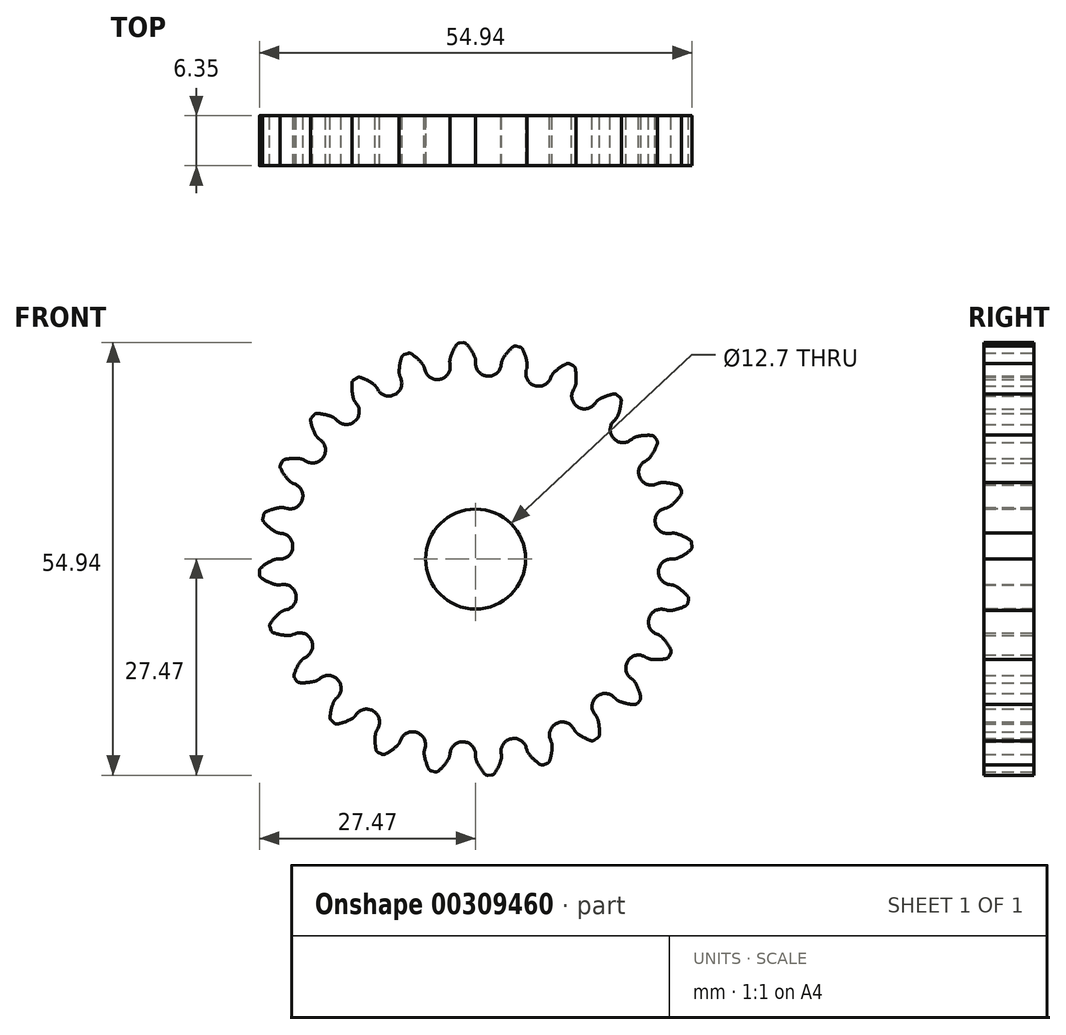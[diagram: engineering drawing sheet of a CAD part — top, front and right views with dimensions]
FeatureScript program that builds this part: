
annotation { "Feature Type Name" : "Feature", "Feature Type Description" : "" }
export const myFeature = defineFeature(function(context is Context, id is Id, definition is map)
    precondition{}
    {
        {
            var Q0;
            Q0=qCreatedBy(makeId("Front.planeOp"),FACE);
            var sketch = newSketch(context, id + "F0", { "sketchPlane" : qUnion([Q0])});
            skArc(sketch, "E0", {"start": v(-4.52, 22.84) * mm, "mid": v(-4.54, 22.83) * mm, "end": v(-4.57, 22.83) * mm});
            skArc(sketch, "E1", {"start": v(-0.14, 25.74) * mm, "mid": v(-0.59, 26.56) * mm, "end": v(-1.15, 27.3) * mm});
            skLineSegment(sketch, "E2", {"start": v(0, 25.08) * mm, "end": v(0, 24.83) * mm});
            skLineSegment(sketch, "E3", {"start": v(-1.56, 27.47) * mm, "end": v(-1.8, 27.46) * mm});
            skLineSegment(sketch, "E4.MirrorCS", {"start": v(-2.04, 27.44) * mm, "end": v(-1.8, 27.46) * mm});
            skArc(sketch, "E5.MirrorCS", {"start": v(-3.22, 25.54) * mm, "mid": v(-2.88, 26.4) * mm, "end": v(-2.43, 27.22) * mm});
            skLineSegment(sketch, "E6.MirrorCS", {"start": v(-3.27, 24.87) * mm, "end": v(-3.24, 24.62) * mm});
            skPoint(sketch, "E7.visualSharp", {"position": v(-3.04, 23.08) * mm});
            skArc(sketch, "E7.filletArc", {"start": v(-4.52, 22.84) * mm, "mid": v(-3.53, 23.47) * mm, "end": v(-3.24, 24.62) * mm});
            skPoint(sketch, "E8.visualSharp", {"position": v(0, 23.28) * mm});
            skArc(sketch, "E8.filletArc", {"start": v(0, 24.83) * mm, "mid": v(0.43, 23.73) * mm, "end": v(1.5, 23.23) * mm});
            skPoint(sketch, "E9.visualSharp", {"position": v(0, 25.4) * mm});
            skArc(sketch, "E9.filletArc", {"start": v(0, 25.08) * mm, "mid": v(-0.04, 25.42) * mm, "end": v(-0.14, 25.74) * mm});
            skPoint(sketch, "E10.visualSharp", {"position": v(-3.32, 25.18) * mm});
            skArc(sketch, "E10.filletArc", {"start": v(-3.22, 25.54) * mm, "mid": v(-3.28, 25.2) * mm, "end": v(-3.27, 24.87) * mm});
            skPoint(sketch, "E11.visualSharp", {"position": v(-2.28, 27.43) * mm});
            skArc(sketch, "E11.filletArc", {"start": v(-2.04, 27.44) * mm, "mid": v(-2.26, 27.38) * mm, "end": v(-2.43, 27.22) * mm});
            skPoint(sketch, "E12.visualSharp", {"position": v(-1.32, 27.49) * mm});
            skArc(sketch, "E12.filletArc", {"start": v(-1.15, 27.3) * mm, "mid": v(-1.33, 27.44) * mm, "end": v(-1.56, 27.47) * mm});
            skArc(sketch, "E13.1.0", {"start": v(-10.27, 20.89) * mm, "mid": v(-9.48, 21.76) * mm, "end": v(-9.5, 22.94) * mm});
            skLineSegment(sketch, "E13.1.1", {"start": v(-9.6, 23.17) * mm, "end": v(-9.5, 22.94) * mm});
            skArc(sketch, "E13.1.2", {"start": v(-9.72, 23.84) * mm, "mid": v(-9.7, 23.5) * mm, "end": v(-9.6, 23.17) * mm});
            skArc(sketch, "E13.1.3", {"start": v(-9.07, 25.98) * mm, "mid": v(-9.27, 25.86) * mm, "end": v(-9.39, 25.66) * mm});
            skArc(sketch, "E13.1.4", {"start": v(-9.72, 23.84) * mm, "mid": v(-9.62, 24.76) * mm, "end": v(-9.39, 25.66) * mm});
            skLineSegment(sketch, "E13.1.5", {"start": v(-9.07, 25.98) * mm, "end": v(-8.84, 26.06) * mm});
            skLineSegment(sketch, "E13.1.6", {"start": v(-8.62, 26.13) * mm, "end": v(-8.84, 26.06) * mm});
            skArc(sketch, "E13.1.7", {"start": v(-8.17, 26.07) * mm, "mid": v(-8.39, 26.16) * mm, "end": v(-8.62, 26.13) * mm});
            skArc(sketch, "E13.1.8", {"start": v(-6.8, 24.83) * mm, "mid": v(-7.44, 25.5) * mm, "end": v(-8.17, 26.07) * mm});
            skArc(sketch, "E13.1.9", {"start": v(-6.5, 24.23) * mm, "mid": v(-6.61, 24.54) * mm, "end": v(-6.8, 24.83) * mm});
            skLineSegment(sketch, "E13.1.10", {"start": v(-6.5, 24.23) * mm, "end": v(-6.43, 23.98) * mm});
            skArc(sketch, "E13.1.11", {"start": v(-6.43, 23.98) * mm, "mid": v(-5.72, 23.04) * mm, "end": v(-4.57, 22.83) * mm});
            skArc(sketch, "E13.2.0", {"start": v(-15.33, 17.52) * mm, "mid": v(-14.8, 18.57) * mm, "end": v(-15.11, 19.7) * mm});
            skLineSegment(sketch, "E13.2.1", {"start": v(-15.27, 19.9) * mm, "end": v(-15.11, 19.7) * mm});
            skArc(sketch, "E13.2.2", {"start": v(-15.56, 20.5) * mm, "mid": v(-15.45, 20.19) * mm, "end": v(-15.27, 19.9) * mm});
            skArc(sketch, "E13.2.3", {"start": v(-15.49, 22.75) * mm, "mid": v(-15.64, 22.58) * mm, "end": v(-15.7, 22.36) * mm});
            skArc(sketch, "E13.2.4", {"start": v(-15.56, 20.5) * mm, "mid": v(-15.7, 21.43) * mm, "end": v(-15.7, 22.36) * mm});
            skLineSegment(sketch, "E13.2.5", {"start": v(-15.49, 22.75) * mm, "end": v(-15.29, 22.88) * mm});
            skLineSegment(sketch, "E13.2.6", {"start": v(-15.09, 23.01) * mm, "end": v(-15.29, 22.88) * mm});
            skArc(sketch, "E13.2.7", {"start": v(-14.64, 23.07) * mm, "mid": v(-14.87, 23.1) * mm, "end": v(-15.09, 23.01) * mm});
            skArc(sketch, "E13.2.8", {"start": v(-13, 22.22) * mm, "mid": v(-13.79, 22.7) * mm, "end": v(-14.64, 23.07) * mm});
            skArc(sketch, "E13.2.9", {"start": v(-12.54, 21.72) * mm, "mid": v(-12.74, 22) * mm, "end": v(-13, 22.22) * mm});
            skLineSegment(sketch, "E13.2.10", {"start": v(-12.54, 21.72) * mm, "end": v(-12.41, 21.5) * mm});
            skArc(sketch, "E13.2.11", {"start": v(-12.41, 21.5) * mm, "mid": v(-11.5, 20.77) * mm, "end": v(-10.32, 20.87) * mm});
            skArc(sketch, "E13.3.0", {"start": v(-19.34, 12.95) * mm, "mid": v(-19.1, 14.1) * mm, "end": v(-19.7, 15.11) * mm});
            skLineSegment(sketch, "E13.3.1", {"start": v(-19.9, 15.27) * mm, "end": v(-19.7, 15.11) * mm});
            skArc(sketch, "E13.3.2", {"start": v(-20.33, 15.78) * mm, "mid": v(-20.14, 15.5) * mm, "end": v(-19.9, 15.27) * mm});
            skArc(sketch, "E13.3.3", {"start": v(-20.84, 17.96) * mm, "mid": v(-20.95, 17.76) * mm, "end": v(-20.96, 17.53) * mm});
            skArc(sketch, "E13.3.4", {"start": v(-20.33, 15.78) * mm, "mid": v(-20.71, 16.63) * mm, "end": v(-20.96, 17.53) * mm});
            skLineSegment(sketch, "E13.3.5", {"start": v(-20.84, 17.96) * mm, "end": v(-20.69, 18.14) * mm});
            skLineSegment(sketch, "E13.3.6", {"start": v(-20.53, 18.32) * mm, "end": v(-20.69, 18.14) * mm});
            skArc(sketch, "E13.3.7", {"start": v(-20.12, 18.5) * mm, "mid": v(-20.34, 18.46) * mm, "end": v(-20.53, 18.32) * mm});
            skArc(sketch, "E13.3.8", {"start": v(-18.3, 18.1) * mm, "mid": v(-19.2, 18.36) * mm, "end": v(-20.12, 18.5) * mm});
            skArc(sketch, "E13.3.9", {"start": v(-17.73, 17.73) * mm, "mid": v(-18, 17.95) * mm, "end": v(-18.3, 18.1) * mm});
            skLineSegment(sketch, "E13.3.10", {"start": v(-17.73, 17.73) * mm, "end": v(-17.56, 17.56) * mm});
            skArc(sketch, "E13.3.11", {"start": v(-17.56, 17.56) * mm, "mid": v(-16.48, 17.09) * mm, "end": v(-15.37, 17.49) * mm});
            skArc(sketch, "E13.4.0", {"start": v(-22.04, 7.5) * mm, "mid": v(-22.1, 8.68) * mm, "end": v(-22.94, 9.5) * mm});
            skLineSegment(sketch, "E13.4.1", {"start": v(-23.17, 9.6) * mm, "end": v(-22.94, 9.5) * mm});
            skArc(sketch, "E13.4.2", {"start": v(-23.73, 9.98) * mm, "mid": v(-23.47, 9.76) * mm, "end": v(-23.17, 9.6) * mm});
            skArc(sketch, "E13.4.3", {"start": v(-24.78, 11.96) * mm, "mid": v(-24.84, 11.73) * mm, "end": v(-24.78, 11.5) * mm});
            skArc(sketch, "E13.4.4", {"start": v(-23.73, 9.98) * mm, "mid": v(-24.31, 10.7) * mm, "end": v(-24.78, 11.5) * mm});
            skLineSegment(sketch, "E13.4.5", {"start": v(-24.78, 11.96) * mm, "end": v(-24.68, 12.17) * mm});
            skLineSegment(sketch, "E13.4.6", {"start": v(-24.57, 12.38) * mm, "end": v(-24.68, 12.17) * mm});
            skArc(sketch, "E13.4.7", {"start": v(-24.22, 12.66) * mm, "mid": v(-24.43, 12.56) * mm, "end": v(-24.57, 12.38) * mm});
            skArc(sketch, "E13.4.8", {"start": v(-22.36, 12.75) * mm, "mid": v(-23.3, 12.77) * mm, "end": v(-24.22, 12.66) * mm});
            skArc(sketch, "E13.4.9", {"start": v(-21.72, 12.54) * mm, "mid": v(-22.03, 12.68) * mm, "end": v(-22.36, 12.75) * mm});
            skLineSegment(sketch, "E13.4.10", {"start": v(-21.72, 12.54) * mm, "end": v(-21.5, 12.41) * mm});
            skArc(sketch, "E13.4.11", {"start": v(-21.5, 12.41) * mm, "mid": v(-20.34, 12.24) * mm, "end": v(-19.37, 12.91) * mm});
            skArc(sketch, "E13.5.0", {"start": v(-23.23, 1.55) * mm, "mid": v(-23.59, 2.67) * mm, "end": v(-24.62, 3.24) * mm});
            skLineSegment(sketch, "E13.5.1", {"start": v(-24.87, 3.27) * mm, "end": v(-24.62, 3.24) * mm});
            skArc(sketch, "E13.5.2", {"start": v(-25.5, 3.5) * mm, "mid": v(-25.2, 3.35) * mm, "end": v(-24.87, 3.27) * mm});
            skArc(sketch, "E13.5.3", {"start": v(-27.03, 5.14) * mm, "mid": v(-27.03, 4.9) * mm, "end": v(-26.92, 4.7) * mm});
            skArc(sketch, "E13.5.4", {"start": v(-25.5, 3.5) * mm, "mid": v(-26.25, 4.05) * mm, "end": v(-26.92, 4.7) * mm});
            skLineSegment(sketch, "E13.5.5", {"start": v(-27.03, 5.14) * mm, "end": v(-26.99, 5.37) * mm});
            skLineSegment(sketch, "E13.5.6", {"start": v(-26.94, 5.6) * mm, "end": v(-26.99, 5.37) * mm});
            skArc(sketch, "E13.5.7", {"start": v(-26.67, 5.96) * mm, "mid": v(-26.85, 5.81) * mm, "end": v(-26.94, 5.6) * mm});
            skArc(sketch, "E13.5.8", {"start": v(-24.9, 6.52) * mm, "mid": v(-25.8, 6.3) * mm, "end": v(-26.67, 5.96) * mm});
            skArc(sketch, "E13.5.9", {"start": v(-24.23, 6.5) * mm, "mid": v(-24.56, 6.54) * mm, "end": v(-24.9, 6.52) * mm});
            skLineSegment(sketch, "E13.5.10", {"start": v(-24.23, 6.5) * mm, "end": v(-23.98, 6.43) * mm});
            skArc(sketch, "E13.5.11", {"start": v(-23.98, 6.43) * mm, "mid": v(-22.81, 6.56) * mm, "end": v(-22.05, 7.46) * mm});
            skArc(sketch, "E13.6.0", {"start": v(-22.84, -4.52) * mm, "mid": v(-23.47, -3.53) * mm, "end": v(-24.62, -3.24) * mm});
            skLineSegment(sketch, "E13.6.1", {"start": v(-24.87, -3.27) * mm, "end": v(-24.62, -3.24) * mm});
            skArc(sketch, "E13.6.2", {"start": v(-25.54, -3.22) * mm, "mid": v(-25.2, -3.28) * mm, "end": v(-24.87, -3.27) * mm});
            skArc(sketch, "E13.6.3", {"start": v(-27.44, -2.04) * mm, "mid": v(-27.38, -2.26) * mm, "end": v(-27.22, -2.43) * mm});
            skArc(sketch, "E13.6.4", {"start": v(-25.54, -3.22) * mm, "mid": v(-26.4, -2.88) * mm, "end": v(-27.22, -2.43) * mm});
            skLineSegment(sketch, "E13.6.5", {"start": v(-27.44, -2.04) * mm, "end": v(-27.46, -1.8) * mm});
            skLineSegment(sketch, "E13.6.6", {"start": v(-27.47, -1.56) * mm, "end": v(-27.46, -1.8) * mm});
            skArc(sketch, "E13.6.7", {"start": v(-27.3, -1.15) * mm, "mid": v(-27.44, -1.33) * mm, "end": v(-27.47, -1.56) * mm});
            skArc(sketch, "E13.6.8", {"start": v(-25.74, -0.14) * mm, "mid": v(-26.56, -0.59) * mm, "end": v(-27.3, -1.15) * mm});
            skArc(sketch, "E13.6.9", {"start": v(-25.08, 0) * mm, "mid": v(-25.42, -0.04) * mm, "end": v(-25.74, -0.14) * mm});
            skLineSegment(sketch, "E13.6.10", {"start": v(-25.08, 0) * mm, "end": v(-24.83, 0) * mm});
            skArc(sketch, "E13.6.11", {"start": v(-24.83, 0) * mm, "mid": v(-23.73, 0.43) * mm, "end": v(-23.23, 1.5) * mm});
            skArc(sketch, "E13.7.0", {"start": v(-20.89, -10.27) * mm, "mid": v(-21.76, -9.48) * mm, "end": v(-22.94, -9.5) * mm});
            skLineSegment(sketch, "E13.7.1", {"start": v(-23.17, -9.6) * mm, "end": v(-22.94, -9.5) * mm});
            skArc(sketch, "E13.7.2", {"start": v(-23.84, -9.72) * mm, "mid": v(-23.5, -9.7) * mm, "end": v(-23.17, -9.6) * mm});
            skArc(sketch, "E13.7.3", {"start": v(-25.98, -9.07) * mm, "mid": v(-25.86, -9.27) * mm, "end": v(-25.66, -9.39) * mm});
            skArc(sketch, "E13.7.4", {"start": v(-23.84, -9.72) * mm, "mid": v(-24.76, -9.62) * mm, "end": v(-25.66, -9.39) * mm});
            skLineSegment(sketch, "E13.7.5", {"start": v(-25.98, -9.07) * mm, "end": v(-26.06, -8.84) * mm});
            skLineSegment(sketch, "E13.7.6", {"start": v(-26.13, -8.62) * mm, "end": v(-26.06, -8.84) * mm});
            skArc(sketch, "E13.7.7", {"start": v(-26.07, -8.17) * mm, "mid": v(-26.16, -8.39) * mm, "end": v(-26.13, -8.62) * mm});
            skArc(sketch, "E13.7.8", {"start": v(-24.83, -6.8) * mm, "mid": v(-25.5, -7.44) * mm, "end": v(-26.07, -8.17) * mm});
            skArc(sketch, "E13.7.9", {"start": v(-24.23, -6.5) * mm, "mid": v(-24.54, -6.61) * mm, "end": v(-24.83, -6.8) * mm});
            skLineSegment(sketch, "E13.7.10", {"start": v(-24.23, -6.5) * mm, "end": v(-23.98, -6.43) * mm});
            skArc(sketch, "E13.7.11", {"start": v(-23.98, -6.43) * mm, "mid": v(-23.04, -5.72) * mm, "end": v(-22.83, -4.57) * mm});
            skArc(sketch, "E13.8.0", {"start": v(-17.52, -15.33) * mm, "mid": v(-18.57, -14.8) * mm, "end": v(-19.7, -15.11) * mm});
            skLineSegment(sketch, "E13.8.1", {"start": v(-19.9, -15.27) * mm, "end": v(-19.7, -15.11) * mm});
            skArc(sketch, "E13.8.2", {"start": v(-20.5, -15.56) * mm, "mid": v(-20.19, -15.45) * mm, "end": v(-19.9, -15.27) * mm});
            skArc(sketch, "E13.8.3", {"start": v(-22.75, -15.49) * mm, "mid": v(-22.58, -15.64) * mm, "end": v(-22.36, -15.7) * mm});
            skArc(sketch, "E13.8.4", {"start": v(-20.5, -15.56) * mm, "mid": v(-21.43, -15.7) * mm, "end": v(-22.36, -15.7) * mm});
            skLineSegment(sketch, "E13.8.5", {"start": v(-22.75, -15.49) * mm, "end": v(-22.88, -15.29) * mm});
            skLineSegment(sketch, "E13.8.6", {"start": v(-23.01, -15.09) * mm, "end": v(-22.88, -15.29) * mm});
            skArc(sketch, "E13.8.7", {"start": v(-23.07, -14.64) * mm, "mid": v(-23.1, -14.87) * mm, "end": v(-23.01, -15.09) * mm});
            skArc(sketch, "E13.8.8", {"start": v(-22.22, -13) * mm, "mid": v(-22.7, -13.79) * mm, "end": v(-23.07, -14.64) * mm});
            skArc(sketch, "E13.8.9", {"start": v(-21.72, -12.54) * mm, "mid": v(-22, -12.74) * mm, "end": v(-22.22, -13) * mm});
            skLineSegment(sketch, "E13.8.10", {"start": v(-21.72, -12.54) * mm, "end": v(-21.5, -12.41) * mm});
            skArc(sketch, "E13.8.11", {"start": v(-21.5, -12.41) * mm, "mid": v(-20.77, -11.5) * mm, "end": v(-20.87, -10.32) * mm});
            skArc(sketch, "E13.9.0", {"start": v(-12.95, -19.34) * mm, "mid": v(-14.1, -19.1) * mm, "end": v(-15.11, -19.7) * mm});
            skLineSegment(sketch, "E13.9.1", {"start": v(-15.27, -19.9) * mm, "end": v(-15.11, -19.7) * mm});
            skArc(sketch, "E13.9.2", {"start": v(-15.78, -20.33) * mm, "mid": v(-15.5, -20.14) * mm, "end": v(-15.27, -19.9) * mm});
            skArc(sketch, "E13.9.3", {"start": v(-17.96, -20.84) * mm, "mid": v(-17.76, -20.95) * mm, "end": v(-17.53, -20.96) * mm});
            skArc(sketch, "E13.9.4", {"start": v(-15.78, -20.33) * mm, "mid": v(-16.63, -20.71) * mm, "end": v(-17.53, -20.96) * mm});
            skLineSegment(sketch, "E13.9.5", {"start": v(-17.96, -20.84) * mm, "end": v(-18.14, -20.69) * mm});
            skLineSegment(sketch, "E13.9.6", {"start": v(-18.32, -20.53) * mm, "end": v(-18.14, -20.69) * mm});
            skArc(sketch, "E13.9.7", {"start": v(-18.5, -20.12) * mm, "mid": v(-18.46, -20.34) * mm, "end": v(-18.32, -20.53) * mm});
            skArc(sketch, "E13.9.8", {"start": v(-18.1, -18.3) * mm, "mid": v(-18.36, -19.2) * mm, "end": v(-18.5, -20.12) * mm});
            skArc(sketch, "E13.9.9", {"start": v(-17.73, -17.73) * mm, "mid": v(-17.95, -18) * mm, "end": v(-18.1, -18.3) * mm});
            skLineSegment(sketch, "E13.9.10", {"start": v(-17.73, -17.73) * mm, "end": v(-17.56, -17.56) * mm});
            skArc(sketch, "E13.9.11", {"start": v(-17.56, -17.56) * mm, "mid": v(-17.09, -16.48) * mm, "end": v(-17.49, -15.37) * mm});
            skArc(sketch, "E13.10.0", {"start": v(-7.5, -22.04) * mm, "mid": v(-8.68, -22.1) * mm, "end": v(-9.5, -22.94) * mm});
            skLineSegment(sketch, "E13.10.1", {"start": v(-9.6, -23.17) * mm, "end": v(-9.5, -22.94) * mm});
            skArc(sketch, "E13.10.2", {"start": v(-9.98, -23.73) * mm, "mid": v(-9.76, -23.47) * mm, "end": v(-9.6, -23.17) * mm});
            skArc(sketch, "E13.10.3", {"start": v(-11.96, -24.78) * mm, "mid": v(-11.73, -24.84) * mm, "end": v(-11.5, -24.78) * mm});
            skArc(sketch, "E13.10.4", {"start": v(-9.98, -23.73) * mm, "mid": v(-10.7, -24.31) * mm, "end": v(-11.5, -24.78) * mm});
            skLineSegment(sketch, "E13.10.5", {"start": v(-11.96, -24.78) * mm, "end": v(-12.17, -24.68) * mm});
            skLineSegment(sketch, "E13.10.6", {"start": v(-12.38, -24.57) * mm, "end": v(-12.17, -24.68) * mm});
            skArc(sketch, "E13.10.7", {"start": v(-12.66, -24.22) * mm, "mid": v(-12.56, -24.43) * mm, "end": v(-12.38, -24.57) * mm});
            skArc(sketch, "E13.10.8", {"start": v(-12.75, -22.36) * mm, "mid": v(-12.77, -23.3) * mm, "end": v(-12.66, -24.22) * mm});
            skArc(sketch, "E13.10.9", {"start": v(-12.54, -21.72) * mm, "mid": v(-12.68, -22.03) * mm, "end": v(-12.75, -22.36) * mm});
            skLineSegment(sketch, "E13.10.10", {"start": v(-12.54, -21.72) * mm, "end": v(-12.41, -21.5) * mm});
            skArc(sketch, "E13.10.11", {"start": v(-12.41, -21.5) * mm, "mid": v(-12.24, -20.34) * mm, "end": v(-12.91, -19.37) * mm});
            skArc(sketch, "E13.11.0", {"start": v(-1.55, -23.23) * mm, "mid": v(-2.67, -23.59) * mm, "end": v(-3.24, -24.62) * mm});
            skLineSegment(sketch, "E13.11.1", {"start": v(-3.27, -24.87) * mm, "end": v(-3.24, -24.62) * mm});
            skArc(sketch, "E13.11.2", {"start": v(-3.5, -25.5) * mm, "mid": v(-3.35, -25.2) * mm, "end": v(-3.27, -24.87) * mm});
            skArc(sketch, "E13.11.3", {"start": v(-5.14, -27.03) * mm, "mid": v(-4.9, -27.03) * mm, "end": v(-4.7, -26.92) * mm});
            skArc(sketch, "E13.11.4", {"start": v(-3.5, -25.5) * mm, "mid": v(-4.05, -26.25) * mm, "end": v(-4.7, -26.92) * mm});
            skLineSegment(sketch, "E13.11.5", {"start": v(-5.14, -27.03) * mm, "end": v(-5.37, -26.99) * mm});
            skLineSegment(sketch, "E13.11.6", {"start": v(-5.6, -26.94) * mm, "end": v(-5.37, -26.99) * mm});
            skArc(sketch, "E13.11.7", {"start": v(-5.96, -26.67) * mm, "mid": v(-5.81, -26.85) * mm, "end": v(-5.6, -26.94) * mm});
            skArc(sketch, "E13.11.8", {"start": v(-6.52, -24.9) * mm, "mid": v(-6.3, -25.8) * mm, "end": v(-5.96, -26.67) * mm});
            skArc(sketch, "E13.11.9", {"start": v(-6.5, -24.23) * mm, "mid": v(-6.54, -24.56) * mm, "end": v(-6.52, -24.9) * mm});
            skLineSegment(sketch, "E13.11.10", {"start": v(-6.5, -24.23) * mm, "end": v(-6.43, -23.98) * mm});
            skArc(sketch, "E13.11.11", {"start": v(-6.43, -23.98) * mm, "mid": v(-6.56, -22.81) * mm, "end": v(-7.46, -22.05) * mm});
            skArc(sketch, "E13.12.0", {"start": v(4.52, -22.84) * mm, "mid": v(3.53, -23.47) * mm, "end": v(3.24, -24.62) * mm});
            skLineSegment(sketch, "E13.12.1", {"start": v(3.27, -24.87) * mm, "end": v(3.24, -24.62) * mm});
            skArc(sketch, "E13.12.2", {"start": v(3.22, -25.54) * mm, "mid": v(3.28, -25.2) * mm, "end": v(3.27, -24.87) * mm});
            skArc(sketch, "E13.12.3", {"start": v(2.04, -27.44) * mm, "mid": v(2.26, -27.38) * mm, "end": v(2.43, -27.22) * mm});
            skArc(sketch, "E13.12.4", {"start": v(3.22, -25.54) * mm, "mid": v(2.88, -26.4) * mm, "end": v(2.43, -27.22) * mm});
            skLineSegment(sketch, "E13.12.5", {"start": v(2.04, -27.44) * mm, "end": v(1.8, -27.46) * mm});
            skLineSegment(sketch, "E13.12.6", {"start": v(1.56, -27.47) * mm, "end": v(1.8, -27.46) * mm});
            skArc(sketch, "E13.12.7", {"start": v(1.15, -27.3) * mm, "mid": v(1.33, -27.44) * mm, "end": v(1.56, -27.47) * mm});
            skArc(sketch, "E13.12.8", {"start": v(0.14, -25.74) * mm, "mid": v(0.59, -26.56) * mm, "end": v(1.15, -27.3) * mm});
            skArc(sketch, "E13.12.9", {"start": v(0, -25.08) * mm, "mid": v(0.04, -25.42) * mm, "end": v(0.14, -25.74) * mm});
            skLineSegment(sketch, "E13.12.10", {"start": v(0, -25.08) * mm, "end": v(0, -24.83) * mm});
            skArc(sketch, "E13.12.11", {"start": v(0, -24.83) * mm, "mid": v(-0.43, -23.73) * mm, "end": v(-1.5, -23.23) * mm});
            skArc(sketch, "E13.13.0", {"start": v(10.27, -20.89) * mm, "mid": v(9.48, -21.76) * mm, "end": v(9.5, -22.94) * mm});
            skLineSegment(sketch, "E13.13.1", {"start": v(9.6, -23.17) * mm, "end": v(9.5, -22.94) * mm});
            skArc(sketch, "E13.13.2", {"start": v(9.72, -23.84) * mm, "mid": v(9.7, -23.5) * mm, "end": v(9.6, -23.17) * mm});
            skArc(sketch, "E13.13.3", {"start": v(9.07, -25.98) * mm, "mid": v(9.27, -25.86) * mm, "end": v(9.39, -25.66) * mm});
            skArc(sketch, "E13.13.4", {"start": v(9.72, -23.84) * mm, "mid": v(9.62, -24.76) * mm, "end": v(9.39, -25.66) * mm});
            skLineSegment(sketch, "E13.13.5", {"start": v(9.07, -25.98) * mm, "end": v(8.84, -26.06) * mm});
            skLineSegment(sketch, "E13.13.6", {"start": v(8.62, -26.13) * mm, "end": v(8.84, -26.06) * mm});
            skArc(sketch, "E13.13.7", {"start": v(8.17, -26.07) * mm, "mid": v(8.39, -26.16) * mm, "end": v(8.62, -26.13) * mm});
            skArc(sketch, "E13.13.8", {"start": v(6.8, -24.83) * mm, "mid": v(7.44, -25.5) * mm, "end": v(8.17, -26.07) * mm});
            skArc(sketch, "E13.13.9", {"start": v(6.5, -24.23) * mm, "mid": v(6.61, -24.54) * mm, "end": v(6.8, -24.83) * mm});
            skLineSegment(sketch, "E13.13.10", {"start": v(6.5, -24.23) * mm, "end": v(6.43, -23.98) * mm});
            skArc(sketch, "E13.13.11", {"start": v(6.43, -23.98) * mm, "mid": v(5.72, -23.04) * mm, "end": v(4.57, -22.83) * mm});
            skArc(sketch, "E13.14.0", {"start": v(15.33, -17.52) * mm, "mid": v(14.8, -18.57) * mm, "end": v(15.11, -19.7) * mm});
            skLineSegment(sketch, "E13.14.1", {"start": v(15.27, -19.9) * mm, "end": v(15.11, -19.7) * mm});
            skArc(sketch, "E13.14.2", {"start": v(15.56, -20.5) * mm, "mid": v(15.45, -20.19) * mm, "end": v(15.27, -19.9) * mm});
            skArc(sketch, "E13.14.3", {"start": v(15.49, -22.75) * mm, "mid": v(15.64, -22.58) * mm, "end": v(15.7, -22.36) * mm});
            skArc(sketch, "E13.14.4", {"start": v(15.56, -20.5) * mm, "mid": v(15.7, -21.43) * mm, "end": v(15.7, -22.36) * mm});
            skLineSegment(sketch, "E13.14.5", {"start": v(15.49, -22.75) * mm, "end": v(15.29, -22.88) * mm});
            skLineSegment(sketch, "E13.14.6", {"start": v(15.09, -23.01) * mm, "end": v(15.29, -22.88) * mm});
            skArc(sketch, "E13.14.7", {"start": v(14.64, -23.07) * mm, "mid": v(14.87, -23.1) * mm, "end": v(15.09, -23.01) * mm});
            skArc(sketch, "E13.14.8", {"start": v(13, -22.22) * mm, "mid": v(13.79, -22.7) * mm, "end": v(14.64, -23.07) * mm});
            skArc(sketch, "E13.14.9", {"start": v(12.54, -21.72) * mm, "mid": v(12.74, -22) * mm, "end": v(13, -22.22) * mm});
            skLineSegment(sketch, "E13.14.10", {"start": v(12.54, -21.72) * mm, "end": v(12.41, -21.5) * mm});
            skArc(sketch, "E13.14.11", {"start": v(12.41, -21.5) * mm, "mid": v(11.5, -20.77) * mm, "end": v(10.32, -20.87) * mm});
            skArc(sketch, "E13.15.0", {"start": v(19.34, -12.95) * mm, "mid": v(19.1, -14.1) * mm, "end": v(19.7, -15.11) * mm});
            skLineSegment(sketch, "E13.15.1", {"start": v(19.9, -15.27) * mm, "end": v(19.7, -15.11) * mm});
            skArc(sketch, "E13.15.2", {"start": v(20.33, -15.78) * mm, "mid": v(20.14, -15.5) * mm, "end": v(19.9, -15.27) * mm});
            skArc(sketch, "E13.15.3", {"start": v(20.84, -17.96) * mm, "mid": v(20.95, -17.76) * mm, "end": v(20.96, -17.53) * mm});
            skArc(sketch, "E13.15.4", {"start": v(20.33, -15.78) * mm, "mid": v(20.71, -16.63) * mm, "end": v(20.96, -17.53) * mm});
            skLineSegment(sketch, "E13.15.5", {"start": v(20.84, -17.96) * mm, "end": v(20.69, -18.14) * mm});
            skLineSegment(sketch, "E13.15.6", {"start": v(20.53, -18.32) * mm, "end": v(20.69, -18.14) * mm});
            skArc(sketch, "E13.15.7", {"start": v(20.12, -18.5) * mm, "mid": v(20.34, -18.46) * mm, "end": v(20.53, -18.32) * mm});
            skArc(sketch, "E13.15.8", {"start": v(18.3, -18.1) * mm, "mid": v(19.2, -18.36) * mm, "end": v(20.12, -18.5) * mm});
            skArc(sketch, "E13.15.9", {"start": v(17.73, -17.73) * mm, "mid": v(18, -17.95) * mm, "end": v(18.3, -18.1) * mm});
            skLineSegment(sketch, "E13.15.10", {"start": v(17.73, -17.73) * mm, "end": v(17.56, -17.56) * mm});
            skArc(sketch, "E13.15.11", {"start": v(17.56, -17.56) * mm, "mid": v(16.48, -17.09) * mm, "end": v(15.37, -17.49) * mm});
            skArc(sketch, "E13.16.0", {"start": v(22.04, -7.5) * mm, "mid": v(22.1, -8.68) * mm, "end": v(22.94, -9.5) * mm});
            skLineSegment(sketch, "E13.16.1", {"start": v(23.17, -9.6) * mm, "end": v(22.94, -9.5) * mm});
            skArc(sketch, "E13.16.2", {"start": v(23.73, -9.98) * mm, "mid": v(23.47, -9.76) * mm, "end": v(23.17, -9.6) * mm});
            skArc(sketch, "E13.16.3", {"start": v(24.78, -11.96) * mm, "mid": v(24.84, -11.73) * mm, "end": v(24.78, -11.5) * mm});
            skArc(sketch, "E13.16.4", {"start": v(23.73, -9.98) * mm, "mid": v(24.31, -10.7) * mm, "end": v(24.78, -11.5) * mm});
            skLineSegment(sketch, "E13.16.5", {"start": v(24.78, -11.96) * mm, "end": v(24.68, -12.17) * mm});
            skLineSegment(sketch, "E13.16.6", {"start": v(24.57, -12.38) * mm, "end": v(24.68, -12.17) * mm});
            skArc(sketch, "E13.16.7", {"start": v(24.22, -12.66) * mm, "mid": v(24.43, -12.56) * mm, "end": v(24.57, -12.38) * mm});
            skArc(sketch, "E13.16.8", {"start": v(22.36, -12.75) * mm, "mid": v(23.3, -12.77) * mm, "end": v(24.22, -12.66) * mm});
            skArc(sketch, "E13.16.9", {"start": v(21.72, -12.54) * mm, "mid": v(22.03, -12.68) * mm, "end": v(22.36, -12.75) * mm});
            skLineSegment(sketch, "E13.16.10", {"start": v(21.72, -12.54) * mm, "end": v(21.5, -12.41) * mm});
            skArc(sketch, "E13.16.11", {"start": v(21.5, -12.41) * mm, "mid": v(20.34, -12.24) * mm, "end": v(19.37, -12.91) * mm});
            skArc(sketch, "E13.17.0", {"start": v(23.23, -1.55) * mm, "mid": v(23.59, -2.67) * mm, "end": v(24.62, -3.24) * mm});
            skLineSegment(sketch, "E13.17.1", {"start": v(24.87, -3.27) * mm, "end": v(24.62, -3.24) * mm});
            skArc(sketch, "E13.17.2", {"start": v(25.5, -3.5) * mm, "mid": v(25.2, -3.35) * mm, "end": v(24.87, -3.27) * mm});
            skArc(sketch, "E13.17.3", {"start": v(27.03, -5.14) * mm, "mid": v(27.03, -4.9) * mm, "end": v(26.92, -4.7) * mm});
            skArc(sketch, "E13.17.4", {"start": v(25.5, -3.5) * mm, "mid": v(26.25, -4.05) * mm, "end": v(26.92, -4.7) * mm});
            skLineSegment(sketch, "E13.17.5", {"start": v(27.03, -5.14) * mm, "end": v(26.99, -5.37) * mm});
            skLineSegment(sketch, "E13.17.6", {"start": v(26.94, -5.6) * mm, "end": v(26.99, -5.37) * mm});
            skArc(sketch, "E13.17.7", {"start": v(26.67, -5.96) * mm, "mid": v(26.85, -5.81) * mm, "end": v(26.94, -5.6) * mm});
            skArc(sketch, "E13.17.8", {"start": v(24.9, -6.52) * mm, "mid": v(25.8, -6.3) * mm, "end": v(26.67, -5.96) * mm});
            skArc(sketch, "E13.17.9", {"start": v(24.23, -6.5) * mm, "mid": v(24.56, -6.54) * mm, "end": v(24.9, -6.52) * mm});
            skLineSegment(sketch, "E13.17.10", {"start": v(24.23, -6.5) * mm, "end": v(23.98, -6.43) * mm});
            skArc(sketch, "E13.17.11", {"start": v(23.98, -6.43) * mm, "mid": v(22.81, -6.56) * mm, "end": v(22.05, -7.46) * mm});
            skArc(sketch, "E13.18.0", {"start": v(22.84, 4.52) * mm, "mid": v(23.47, 3.53) * mm, "end": v(24.62, 3.24) * mm});
            skLineSegment(sketch, "E13.18.1", {"start": v(24.87, 3.27) * mm, "end": v(24.62, 3.24) * mm});
            skArc(sketch, "E13.18.2", {"start": v(25.54, 3.22) * mm, "mid": v(25.2, 3.28) * mm, "end": v(24.87, 3.27) * mm});
            skArc(sketch, "E13.18.3", {"start": v(27.44, 2.04) * mm, "mid": v(27.38, 2.26) * mm, "end": v(27.22, 2.43) * mm});
            skArc(sketch, "E13.18.4", {"start": v(25.54, 3.22) * mm, "mid": v(26.4, 2.88) * mm, "end": v(27.22, 2.43) * mm});
            skLineSegment(sketch, "E13.18.5", {"start": v(27.44, 2.04) * mm, "end": v(27.46, 1.8) * mm});
            skLineSegment(sketch, "E13.18.6", {"start": v(27.47, 1.56) * mm, "end": v(27.46, 1.8) * mm});
            skArc(sketch, "E13.18.7", {"start": v(27.3, 1.15) * mm, "mid": v(27.44, 1.33) * mm, "end": v(27.47, 1.56) * mm});
            skArc(sketch, "E13.18.8", {"start": v(25.74, 0.14) * mm, "mid": v(26.56, 0.59) * mm, "end": v(27.3, 1.15) * mm});
            skArc(sketch, "E13.18.9", {"start": v(25.08, 0) * mm, "mid": v(25.42, 0.04) * mm, "end": v(25.74, 0.14) * mm});
            skLineSegment(sketch, "E13.18.10", {"start": v(25.08, 0) * mm, "end": v(24.83, 0) * mm});
            skArc(sketch, "E13.18.11", {"start": v(24.83, 0) * mm, "mid": v(23.73, -0.43) * mm, "end": v(23.23, -1.5) * mm});
            skArc(sketch, "E13.19.0", {"start": v(20.89, 10.27) * mm, "mid": v(21.76, 9.48) * mm, "end": v(22.94, 9.5) * mm});
            skLineSegment(sketch, "E13.19.1", {"start": v(23.17, 9.6) * mm, "end": v(22.94, 9.5) * mm});
            skArc(sketch, "E13.19.2", {"start": v(23.84, 9.72) * mm, "mid": v(23.5, 9.7) * mm, "end": v(23.17, 9.6) * mm});
            skArc(sketch, "E13.19.3", {"start": v(25.98, 9.07) * mm, "mid": v(25.86, 9.27) * mm, "end": v(25.66, 9.39) * mm});
            skArc(sketch, "E13.19.4", {"start": v(23.84, 9.72) * mm, "mid": v(24.76, 9.62) * mm, "end": v(25.66, 9.39) * mm});
            skLineSegment(sketch, "E13.19.5", {"start": v(25.98, 9.07) * mm, "end": v(26.06, 8.84) * mm});
            skLineSegment(sketch, "E13.19.6", {"start": v(26.13, 8.62) * mm, "end": v(26.06, 8.84) * mm});
            skArc(sketch, "E13.19.7", {"start": v(26.07, 8.17) * mm, "mid": v(26.16, 8.39) * mm, "end": v(26.13, 8.62) * mm});
            skArc(sketch, "E13.19.8", {"start": v(24.83, 6.8) * mm, "mid": v(25.5, 7.44) * mm, "end": v(26.07, 8.17) * mm});
            skArc(sketch, "E13.19.9", {"start": v(24.23, 6.5) * mm, "mid": v(24.54, 6.61) * mm, "end": v(24.83, 6.8) * mm});
            skLineSegment(sketch, "E13.19.10", {"start": v(24.23, 6.5) * mm, "end": v(23.98, 6.43) * mm});
            skArc(sketch, "E13.19.11", {"start": v(23.98, 6.43) * mm, "mid": v(23.04, 5.72) * mm, "end": v(22.83, 4.57) * mm});
            skArc(sketch, "E13.20.0", {"start": v(17.52, 15.33) * mm, "mid": v(18.57, 14.8) * mm, "end": v(19.7, 15.11) * mm});
            skLineSegment(sketch, "E13.20.1", {"start": v(19.9, 15.27) * mm, "end": v(19.7, 15.11) * mm});
            skArc(sketch, "E13.20.2", {"start": v(20.5, 15.56) * mm, "mid": v(20.19, 15.45) * mm, "end": v(19.9, 15.27) * mm});
            skArc(sketch, "E13.20.3", {"start": v(22.75, 15.49) * mm, "mid": v(22.58, 15.64) * mm, "end": v(22.36, 15.7) * mm});
            skArc(sketch, "E13.20.4", {"start": v(20.5, 15.56) * mm, "mid": v(21.43, 15.7) * mm, "end": v(22.36, 15.7) * mm});
            skLineSegment(sketch, "E13.20.5", {"start": v(22.75, 15.49) * mm, "end": v(22.88, 15.29) * mm});
            skLineSegment(sketch, "E13.20.6", {"start": v(23.01, 15.09) * mm, "end": v(22.88, 15.29) * mm});
            skArc(sketch, "E13.20.7", {"start": v(23.07, 14.64) * mm, "mid": v(23.1, 14.87) * mm, "end": v(23.01, 15.09) * mm});
            skArc(sketch, "E13.20.8", {"start": v(22.22, 13) * mm, "mid": v(22.7, 13.79) * mm, "end": v(23.07, 14.64) * mm});
            skArc(sketch, "E13.20.9", {"start": v(21.72, 12.54) * mm, "mid": v(22, 12.74) * mm, "end": v(22.22, 13) * mm});
            skLineSegment(sketch, "E13.20.10", {"start": v(21.72, 12.54) * mm, "end": v(21.5, 12.41) * mm});
            skArc(sketch, "E13.20.11", {"start": v(21.5, 12.41) * mm, "mid": v(20.77, 11.5) * mm, "end": v(20.87, 10.32) * mm});
            skArc(sketch, "E13.21.0", {"start": v(12.95, 19.34) * mm, "mid": v(14.1, 19.1) * mm, "end": v(15.11, 19.7) * mm});
            skLineSegment(sketch, "E13.21.1", {"start": v(15.27, 19.9) * mm, "end": v(15.11, 19.7) * mm});
            skArc(sketch, "E13.21.2", {"start": v(15.78, 20.33) * mm, "mid": v(15.5, 20.14) * mm, "end": v(15.27, 19.9) * mm});
            skArc(sketch, "E13.21.3", {"start": v(17.96, 20.84) * mm, "mid": v(17.76, 20.95) * mm, "end": v(17.53, 20.96) * mm});
            skArc(sketch, "E13.21.4", {"start": v(15.78, 20.33) * mm, "mid": v(16.63, 20.71) * mm, "end": v(17.53, 20.96) * mm});
            skLineSegment(sketch, "E13.21.5", {"start": v(17.96, 20.84) * mm, "end": v(18.14, 20.69) * mm});
            skLineSegment(sketch, "E13.21.6", {"start": v(18.32, 20.53) * mm, "end": v(18.14, 20.69) * mm});
            skArc(sketch, "E13.21.7", {"start": v(18.5, 20.12) * mm, "mid": v(18.46, 20.34) * mm, "end": v(18.32, 20.53) * mm});
            skArc(sketch, "E13.21.8", {"start": v(18.1, 18.3) * mm, "mid": v(18.36, 19.2) * mm, "end": v(18.5, 20.12) * mm});
            skArc(sketch, "E13.21.9", {"start": v(17.73, 17.73) * mm, "mid": v(17.95, 18) * mm, "end": v(18.1, 18.3) * mm});
            skLineSegment(sketch, "E13.21.10", {"start": v(17.73, 17.73) * mm, "end": v(17.56, 17.56) * mm});
            skArc(sketch, "E13.21.11", {"start": v(17.56, 17.56) * mm, "mid": v(17.09, 16.48) * mm, "end": v(17.49, 15.37) * mm});
            skArc(sketch, "E13.22.0", {"start": v(7.5, 22.04) * mm, "mid": v(8.68, 22.1) * mm, "end": v(9.5, 22.94) * mm});
            skLineSegment(sketch, "E13.22.1", {"start": v(9.6, 23.17) * mm, "end": v(9.5, 22.94) * mm});
            skArc(sketch, "E13.22.2", {"start": v(9.98, 23.73) * mm, "mid": v(9.76, 23.47) * mm, "end": v(9.6, 23.17) * mm});
            skArc(sketch, "E13.22.3", {"start": v(11.96, 24.78) * mm, "mid": v(11.73, 24.84) * mm, "end": v(11.5, 24.78) * mm});
            skArc(sketch, "E13.22.4", {"start": v(9.98, 23.73) * mm, "mid": v(10.7, 24.31) * mm, "end": v(11.5, 24.78) * mm});
            skLineSegment(sketch, "E13.22.5", {"start": v(11.96, 24.78) * mm, "end": v(12.17, 24.68) * mm});
            skLineSegment(sketch, "E13.22.6", {"start": v(12.38, 24.57) * mm, "end": v(12.17, 24.68) * mm});
            skArc(sketch, "E13.22.7", {"start": v(12.66, 24.22) * mm, "mid": v(12.56, 24.43) * mm, "end": v(12.38, 24.57) * mm});
            skArc(sketch, "E13.22.8", {"start": v(12.75, 22.36) * mm, "mid": v(12.77, 23.3) * mm, "end": v(12.66, 24.22) * mm});
            skArc(sketch, "E13.22.9", {"start": v(12.54, 21.72) * mm, "mid": v(12.68, 22.03) * mm, "end": v(12.75, 22.36) * mm});
            skLineSegment(sketch, "E13.22.10", {"start": v(12.54, 21.72) * mm, "end": v(12.41, 21.5) * mm});
            skArc(sketch, "E13.22.11", {"start": v(12.41, 21.5) * mm, "mid": v(12.24, 20.34) * mm, "end": v(12.91, 19.37) * mm});
            skArc(sketch, "E13.23.0", {"start": v(1.55, 23.23) * mm, "mid": v(2.67, 23.59) * mm, "end": v(3.24, 24.62) * mm});
            skLineSegment(sketch, "E13.23.1", {"start": v(3.27, 24.87) * mm, "end": v(3.24, 24.62) * mm});
            skArc(sketch, "E13.23.2", {"start": v(3.5, 25.5) * mm, "mid": v(3.35, 25.2) * mm, "end": v(3.27, 24.87) * mm});
            skArc(sketch, "E13.23.3", {"start": v(5.14, 27.03) * mm, "mid": v(4.9, 27.03) * mm, "end": v(4.7, 26.92) * mm});
            skArc(sketch, "E13.23.4", {"start": v(3.5, 25.5) * mm, "mid": v(4.05, 26.25) * mm, "end": v(4.7, 26.92) * mm});
            skLineSegment(sketch, "E13.23.5", {"start": v(5.14, 27.03) * mm, "end": v(5.37, 26.99) * mm});
            skLineSegment(sketch, "E13.23.6", {"start": v(5.6, 26.94) * mm, "end": v(5.37, 26.99) * mm});
            skArc(sketch, "E13.23.7", {"start": v(5.96, 26.67) * mm, "mid": v(5.81, 26.85) * mm, "end": v(5.6, 26.94) * mm});
            skArc(sketch, "E13.23.8", {"start": v(6.52, 24.9) * mm, "mid": v(6.3, 25.8) * mm, "end": v(5.96, 26.67) * mm});
            skArc(sketch, "E13.23.9", {"start": v(6.5, 24.23) * mm, "mid": v(6.54, 24.56) * mm, "end": v(6.52, 24.9) * mm});
            skLineSegment(sketch, "E13.23.10", {"start": v(6.5, 24.23) * mm, "end": v(6.43, 23.98) * mm});
            skArc(sketch, "E13.23.11", {"start": v(6.43, 23.98) * mm, "mid": v(6.56, 22.81) * mm, "end": v(7.46, 22.05) * mm});
            skArc(sketch, "E14.trimOffspring", {"start": v(-10.27, 20.89) * mm, "mid": v(-10.3, 20.88) * mm, "end": v(-10.32, 20.87) * mm});
            skArc(sketch, "E15.trimOffspring", {"start": v(-15.33, 17.52) * mm, "mid": v(-15.35, 17.5) * mm, "end": v(-15.37, 17.49) * mm});
            skArc(sketch, "E16.trimOffspring", {"start": v(1.55, 23.23) * mm, "mid": v(1.52, 23.23) * mm, "end": v(1.5, 23.23) * mm});
            skArc(sketch, "E17.trimOffspring", {"start": v(7.5, 22.04) * mm, "mid": v(7.48, 22.04) * mm, "end": v(7.46, 22.05) * mm});
            skArc(sketch, "E18.trimOffspring", {"start": v(12.95, 19.34) * mm, "mid": v(12.93, 19.36) * mm, "end": v(12.91, 19.37) * mm});
            skArc(sketch, "E19.trimOffspring", {"start": v(17.52, 15.33) * mm, "mid": v(17.5, 15.35) * mm, "end": v(17.49, 15.37) * mm});
            skArc(sketch, "E20.trimOffspring", {"start": v(20.89, 10.27) * mm, "mid": v(20.88, 10.3) * mm, "end": v(20.87, 10.32) * mm});
            skArc(sketch, "E21.trimOffspring", {"start": v(22.84, 4.52) * mm, "mid": v(22.83, 4.54) * mm, "end": v(22.83, 4.57) * mm});
            skArc(sketch, "E22.trimOffspring", {"start": v(23.23, -1.55) * mm, "mid": v(23.23, -1.52) * mm, "end": v(23.23, -1.5) * mm});
            skArc(sketch, "E23.trimOffspring", {"start": v(-19.34, 12.95) * mm, "mid": v(-19.36, 12.93) * mm, "end": v(-19.37, 12.91) * mm});
            skArc(sketch, "E24.trimOffspring", {"start": v(-22.04, 7.5) * mm, "mid": v(-22.04, 7.48) * mm, "end": v(-22.05, 7.46) * mm});
            skArc(sketch, "E25.trimOffspring", {"start": v(-23.23, 1.55) * mm, "mid": v(-23.23, 1.52) * mm, "end": v(-23.23, 1.5) * mm});
            skArc(sketch, "E26.trimOffspring", {"start": v(-22.84, -4.52) * mm, "mid": v(-22.83, -4.54) * mm, "end": v(-22.83, -4.57) * mm});
            skArc(sketch, "E27.trimOffspring", {"start": v(-20.89, -10.27) * mm, "mid": v(-20.88, -10.3) * mm, "end": v(-20.87, -10.32) * mm});
            skArc(sketch, "E28.trimOffspring", {"start": v(-17.52, -15.33) * mm, "mid": v(-17.5, -15.35) * mm, "end": v(-17.49, -15.37) * mm});
            skArc(sketch, "E29.trimOffspring", {"start": v(-12.95, -19.34) * mm, "mid": v(-12.93, -19.36) * mm, "end": v(-12.91, -19.37) * mm});
            skArc(sketch, "E30.trimOffspring", {"start": v(-7.5, -22.04) * mm, "mid": v(-7.48, -22.04) * mm, "end": v(-7.46, -22.05) * mm});
            skArc(sketch, "E31.trimOffspring", {"start": v(-1.55, -23.23) * mm, "mid": v(-1.52, -23.23) * mm, "end": v(-1.5, -23.23) * mm});
            skArc(sketch, "E32.trimOffspring", {"start": v(4.52, -22.84) * mm, "mid": v(4.54, -22.83) * mm, "end": v(4.57, -22.83) * mm});
            skArc(sketch, "E33.trimOffspring", {"start": v(10.27, -20.89) * mm, "mid": v(10.3, -20.88) * mm, "end": v(10.32, -20.87) * mm});
            skArc(sketch, "E34.trimOffspring", {"start": v(15.33, -17.52) * mm, "mid": v(15.35, -17.5) * mm, "end": v(15.37, -17.49) * mm});
            skArc(sketch, "E35.trimOffspring", {"start": v(19.34, -12.95) * mm, "mid": v(19.36, -12.93) * mm, "end": v(19.37, -12.91) * mm});
            skArc(sketch, "E36.trimOffspring", {"start": v(22.04, -7.5) * mm, "mid": v(22.04, -7.48) * mm, "end": v(22.05, -7.46) * mm});
            skSolve(sketch);
        }
        {
            var Q0;
            Q0 = qSketchRegion(id + "F0", true);
            var Q1;
            Q1=makeQuery(id+"F0.imprint","IMPRINT",FACE,{"disambiguationData":[TD([[makeQuery(id+"F0.imprint","IMPRINT",EDGE,{"derivedFrom":sQuery(id+"F0.wireOp",EDGE,"E0")}),1.0]])]});
            extrude(context, id + "F1", {"entities" : qUnion([Q0, Q1]), "depth" : 6.35 * mm});
        }
        {
            var Q0;
            Q0=makeQuery(id+"F1.opExtrude","CAP_FACE",FACE,{"disambiguationData":[OSD([sQuery(id+"F0.wireOp",EDGE,"E0"),sQuery(id+"F0.wireOp",EDGE,"E1"),sQuery(id+"F0.wireOp",EDGE,"E2"),sQuery(id+"F0.wireOp",EDGE,"E3"),sQuery(id+"F0.wireOp",EDGE,"E4.MirrorCS"),sQuery(id+"F0.wireOp",EDGE,"E5.MirrorCS"),sQuery(id+"F0.wireOp",EDGE,"E6.MirrorCS"),sQuery(id+"F0.wireOp",EDGE,"E7.filletArc"),sQuery(id+"F0.wireOp",EDGE,"E8.filletArc"),sQuery(id+"F0.wireOp",EDGE,"E9.filletArc"),sQuery(id+"F0.wireOp",EDGE,"E10.filletArc"),sQuery(id+"F0.wireOp",EDGE,"E11.filletArc"),sQuery(id+"F0.wireOp",EDGE,"E12.filletArc"),sQuery(id+"F0.wireOp",EDGE,"E13.1.0"),sQuery(id+"F0.wireOp",EDGE,"E13.1.1"),sQuery(id+"F0.wireOp",EDGE,"E13.1.2"),sQuery(id+"F0.wireOp",EDGE,"E13.1.3"),sQuery(id+"F0.wireOp",EDGE,"E13.1.4"),sQuery(id+"F0.wireOp",EDGE,"E13.1.5"),sQuery(id+"F0.wireOp",EDGE,"E13.1.6"),sQuery(id+"F0.wireOp",EDGE,"E13.1.7"),sQuery(id+"F0.wireOp",EDGE,"E13.1.8"),sQuery(id+"F0.wireOp",EDGE,"E13.1.9"),sQuery(id+"F0.wireOp",EDGE,"E13.1.10"),sQuery(id+"F0.wireOp",EDGE,"E13.1.11"),sQuery(id+"F0.wireOp",EDGE,"E13.2.0"),sQuery(id+"F0.wireOp",EDGE,"E13.2.1"),sQuery(id+"F0.wireOp",EDGE,"E13.2.2"),sQuery(id+"F0.wireOp",EDGE,"E13.2.3"),sQuery(id+"F0.wireOp",EDGE,"E13.2.4"),sQuery(id+"F0.wireOp",EDGE,"E13.2.5"),sQuery(id+"F0.wireOp",EDGE,"E13.2.6"),sQuery(id+"F0.wireOp",EDGE,"E13.2.7"),sQuery(id+"F0.wireOp",EDGE,"E13.2.8"),sQuery(id+"F0.wireOp",EDGE,"E13.2.9"),sQuery(id+"F0.wireOp",EDGE,"E13.2.10"),sQuery(id+"F0.wireOp",EDGE,"E13.2.11"),sQuery(id+"F0.wireOp",EDGE,"E13.3.0"),sQuery(id+"F0.wireOp",EDGE,"E13.3.1"),sQuery(id+"F0.wireOp",EDGE,"E13.3.2"),sQuery(id+"F0.wireOp",EDGE,"E13.3.3"),sQuery(id+"F0.wireOp",EDGE,"E13.3.4"),sQuery(id+"F0.wireOp",EDGE,"E13.3.5"),sQuery(id+"F0.wireOp",EDGE,"E13.3.6"),sQuery(id+"F0.wireOp",EDGE,"E13.3.7"),sQuery(id+"F0.wireOp",EDGE,"E13.3.8"),sQuery(id+"F0.wireOp",EDGE,"E13.3.9"),sQuery(id+"F0.wireOp",EDGE,"E13.3.10"),sQuery(id+"F0.wireOp",EDGE,"E13.3.11"),sQuery(id+"F0.wireOp",EDGE,"E13.4.0"),sQuery(id+"F0.wireOp",EDGE,"E13.4.1"),sQuery(id+"F0.wireOp",EDGE,"E13.4.2"),sQuery(id+"F0.wireOp",EDGE,"E13.4.3"),sQuery(id+"F0.wireOp",EDGE,"E13.4.4"),sQuery(id+"F0.wireOp",EDGE,"E13.4.5"),sQuery(id+"F0.wireOp",EDGE,"E13.4.6"),sQuery(id+"F0.wireOp",EDGE,"E13.4.7"),sQuery(id+"F0.wireOp",EDGE,"E13.4.8"),sQuery(id+"F0.wireOp",EDGE,"E13.4.9"),sQuery(id+"F0.wireOp",EDGE,"E13.4.10"),sQuery(id+"F0.wireOp",EDGE,"E13.4.11"),sQuery(id+"F0.wireOp",EDGE,"E13.5.0"),sQuery(id+"F0.wireOp",EDGE,"E13.5.1"),sQuery(id+"F0.wireOp",EDGE,"E13.5.2"),sQuery(id+"F0.wireOp",EDGE,"E13.5.3"),sQuery(id+"F0.wireOp",EDGE,"E13.5.4"),sQuery(id+"F0.wireOp",EDGE,"E13.5.5"),sQuery(id+"F0.wireOp",EDGE,"E13.5.6"),sQuery(id+"F0.wireOp",EDGE,"E13.5.7"),sQuery(id+"F0.wireOp",EDGE,"E13.5.8"),sQuery(id+"F0.wireOp",EDGE,"E13.5.9"),sQuery(id+"F0.wireOp",EDGE,"E13.5.10"),sQuery(id+"F0.wireOp",EDGE,"E13.5.11"),sQuery(id+"F0.wireOp",EDGE,"E13.6.0"),sQuery(id+"F0.wireOp",EDGE,"E13.6.1"),sQuery(id+"F0.wireOp",EDGE,"E13.6.2"),sQuery(id+"F0.wireOp",EDGE,"E13.6.3"),sQuery(id+"F0.wireOp",EDGE,"E13.6.4"),sQuery(id+"F0.wireOp",EDGE,"E13.6.5"),sQuery(id+"F0.wireOp",EDGE,"E13.6.6"),sQuery(id+"F0.wireOp",EDGE,"E13.6.7"),sQuery(id+"F0.wireOp",EDGE,"E13.6.8"),sQuery(id+"F0.wireOp",EDGE,"E13.6.9"),sQuery(id+"F0.wireOp",EDGE,"E13.6.10"),sQuery(id+"F0.wireOp",EDGE,"E13.6.11"),sQuery(id+"F0.wireOp",EDGE,"E13.7.0"),sQuery(id+"F0.wireOp",EDGE,"E13.7.1"),sQuery(id+"F0.wireOp",EDGE,"E13.7.2"),sQuery(id+"F0.wireOp",EDGE,"E13.7.3"),sQuery(id+"F0.wireOp",EDGE,"E13.7.4"),sQuery(id+"F0.wireOp",EDGE,"E13.7.5"),sQuery(id+"F0.wireOp",EDGE,"E13.7.6"),sQuery(id+"F0.wireOp",EDGE,"E13.7.7"),sQuery(id+"F0.wireOp",EDGE,"E13.7.8"),sQuery(id+"F0.wireOp",EDGE,"E13.7.9"),sQuery(id+"F0.wireOp",EDGE,"E13.7.10"),sQuery(id+"F0.wireOp",EDGE,"E13.7.11"),sQuery(id+"F0.wireOp",EDGE,"E13.8.0"),sQuery(id+"F0.wireOp",EDGE,"E13.8.1"),sQuery(id+"F0.wireOp",EDGE,"E13.8.2"),sQuery(id+"F0.wireOp",EDGE,"E13.8.3"),sQuery(id+"F0.wireOp",EDGE,"E13.8.4"),sQuery(id+"F0.wireOp",EDGE,"E13.8.5"),sQuery(id+"F0.wireOp",EDGE,"E13.8.6"),sQuery(id+"F0.wireOp",EDGE,"E13.8.7"),sQuery(id+"F0.wireOp",EDGE,"E13.8.8"),sQuery(id+"F0.wireOp",EDGE,"E13.8.9"),sQuery(id+"F0.wireOp",EDGE,"E13.8.10"),sQuery(id+"F0.wireOp",EDGE,"E13.8.11"),sQuery(id+"F0.wireOp",EDGE,"E13.9.0"),sQuery(id+"F0.wireOp",EDGE,"E13.9.1"),sQuery(id+"F0.wireOp",EDGE,"E13.9.2"),sQuery(id+"F0.wireOp",EDGE,"E13.9.3"),sQuery(id+"F0.wireOp",EDGE,"E13.9.4"),sQuery(id+"F0.wireOp",EDGE,"E13.9.5"),sQuery(id+"F0.wireOp",EDGE,"E13.9.6"),sQuery(id+"F0.wireOp",EDGE,"E13.9.7"),sQuery(id+"F0.wireOp",EDGE,"E13.9.8"),sQuery(id+"F0.wireOp",EDGE,"E13.9.9"),sQuery(id+"F0.wireOp",EDGE,"E13.9.10"),sQuery(id+"F0.wireOp",EDGE,"E13.9.11"),sQuery(id+"F0.wireOp",EDGE,"E13.10.0"),sQuery(id+"F0.wireOp",EDGE,"E13.10.1"),sQuery(id+"F0.wireOp",EDGE,"E13.10.2"),sQuery(id+"F0.wireOp",EDGE,"E13.10.3"),sQuery(id+"F0.wireOp",EDGE,"E13.10.4"),sQuery(id+"F0.wireOp",EDGE,"E13.10.5"),sQuery(id+"F0.wireOp",EDGE,"E13.10.6"),sQuery(id+"F0.wireOp",EDGE,"E13.10.7"),sQuery(id+"F0.wireOp",EDGE,"E13.10.8"),sQuery(id+"F0.wireOp",EDGE,"E13.10.9"),sQuery(id+"F0.wireOp",EDGE,"E13.10.10"),sQuery(id+"F0.wireOp",EDGE,"E13.10.11"),sQuery(id+"F0.wireOp",EDGE,"E13.11.0"),sQuery(id+"F0.wireOp",EDGE,"E13.11.1"),sQuery(id+"F0.wireOp",EDGE,"E13.11.2"),sQuery(id+"F0.wireOp",EDGE,"E13.11.3"),sQuery(id+"F0.wireOp",EDGE,"E13.11.4"),sQuery(id+"F0.wireOp",EDGE,"E13.11.5"),sQuery(id+"F0.wireOp",EDGE,"E13.11.6"),sQuery(id+"F0.wireOp",EDGE,"E13.11.7"),sQuery(id+"F0.wireOp",EDGE,"E13.11.8"),sQuery(id+"F0.wireOp",EDGE,"E13.11.9"),sQuery(id+"F0.wireOp",EDGE,"E13.11.10"),sQuery(id+"F0.wireOp",EDGE,"E13.11.11"),sQuery(id+"F0.wireOp",EDGE,"E13.12.0"),sQuery(id+"F0.wireOp",EDGE,"E13.12.1"),sQuery(id+"F0.wireOp",EDGE,"E13.12.2"),sQuery(id+"F0.wireOp",EDGE,"E13.12.3"),sQuery(id+"F0.wireOp",EDGE,"E13.12.4"),sQuery(id+"F0.wireOp",EDGE,"E13.12.5"),sQuery(id+"F0.wireOp",EDGE,"E13.12.6"),sQuery(id+"F0.wireOp",EDGE,"E13.12.7"),sQuery(id+"F0.wireOp",EDGE,"E13.12.8"),sQuery(id+"F0.wireOp",EDGE,"E13.12.9"),sQuery(id+"F0.wireOp",EDGE,"E13.12.10"),sQuery(id+"F0.wireOp",EDGE,"E13.12.11"),sQuery(id+"F0.wireOp",EDGE,"E13.13.0"),sQuery(id+"F0.wireOp",EDGE,"E13.13.1"),sQuery(id+"F0.wireOp",EDGE,"E13.13.2"),sQuery(id+"F0.wireOp",EDGE,"E13.13.3"),sQuery(id+"F0.wireOp",EDGE,"E13.13.4"),sQuery(id+"F0.wireOp",EDGE,"E13.13.5"),sQuery(id+"F0.wireOp",EDGE,"E13.13.6"),sQuery(id+"F0.wireOp",EDGE,"E13.13.7"),sQuery(id+"F0.wireOp",EDGE,"E13.13.8"),sQuery(id+"F0.wireOp",EDGE,"E13.13.9"),sQuery(id+"F0.wireOp",EDGE,"E13.13.10"),sQuery(id+"F0.wireOp",EDGE,"E13.13.11"),sQuery(id+"F0.wireOp",EDGE,"E13.14.0"),sQuery(id+"F0.wireOp",EDGE,"E13.14.1"),sQuery(id+"F0.wireOp",EDGE,"E13.14.2"),sQuery(id+"F0.wireOp",EDGE,"E13.14.3"),sQuery(id+"F0.wireOp",EDGE,"E13.14.4"),sQuery(id+"F0.wireOp",EDGE,"E13.14.5"),sQuery(id+"F0.wireOp",EDGE,"E13.14.6"),sQuery(id+"F0.wireOp",EDGE,"E13.14.7"),sQuery(id+"F0.wireOp",EDGE,"E13.14.8"),sQuery(id+"F0.wireOp",EDGE,"E13.14.9"),sQuery(id+"F0.wireOp",EDGE,"E13.14.10"),sQuery(id+"F0.wireOp",EDGE,"E13.14.11"),sQuery(id+"F0.wireOp",EDGE,"E13.15.0"),sQuery(id+"F0.wireOp",EDGE,"E13.15.1"),sQuery(id+"F0.wireOp",EDGE,"E13.15.2"),sQuery(id+"F0.wireOp",EDGE,"E13.15.3"),sQuery(id+"F0.wireOp",EDGE,"E13.15.4"),sQuery(id+"F0.wireOp",EDGE,"E13.15.5"),sQuery(id+"F0.wireOp",EDGE,"E13.15.6"),sQuery(id+"F0.wireOp",EDGE,"E13.15.7"),sQuery(id+"F0.wireOp",EDGE,"E13.15.8"),sQuery(id+"F0.wireOp",EDGE,"E13.15.9"),sQuery(id+"F0.wireOp",EDGE,"E13.15.10"),sQuery(id+"F0.wireOp",EDGE,"E13.15.11"),sQuery(id+"F0.wireOp",EDGE,"E13.16.0"),sQuery(id+"F0.wireOp",EDGE,"E13.16.1"),sQuery(id+"F0.wireOp",EDGE,"E13.16.2"),sQuery(id+"F0.wireOp",EDGE,"E13.16.3"),sQuery(id+"F0.wireOp",EDGE,"E13.16.4"),sQuery(id+"F0.wireOp",EDGE,"E13.16.5"),sQuery(id+"F0.wireOp",EDGE,"E13.16.6"),sQuery(id+"F0.wireOp",EDGE,"E13.16.7"),sQuery(id+"F0.wireOp",EDGE,"E13.16.8"),sQuery(id+"F0.wireOp",EDGE,"E13.16.9"),sQuery(id+"F0.wireOp",EDGE,"E13.16.10"),sQuery(id+"F0.wireOp",EDGE,"E13.16.11"),sQuery(id+"F0.wireOp",EDGE,"E13.17.0"),sQuery(id+"F0.wireOp",EDGE,"E13.17.1"),sQuery(id+"F0.wireOp",EDGE,"E13.17.2"),sQuery(id+"F0.wireOp",EDGE,"E13.17.3"),sQuery(id+"F0.wireOp",EDGE,"E13.17.4"),sQuery(id+"F0.wireOp",EDGE,"E13.17.5"),sQuery(id+"F0.wireOp",EDGE,"E13.17.6"),sQuery(id+"F0.wireOp",EDGE,"E13.17.7"),sQuery(id+"F0.wireOp",EDGE,"E13.17.8"),sQuery(id+"F0.wireOp",EDGE,"E13.17.9"),sQuery(id+"F0.wireOp",EDGE,"E13.17.10"),sQuery(id+"F0.wireOp",EDGE,"E13.17.11"),sQuery(id+"F0.wireOp",EDGE,"E13.18.0"),sQuery(id+"F0.wireOp",EDGE,"E13.18.1"),sQuery(id+"F0.wireOp",EDGE,"E13.18.2"),sQuery(id+"F0.wireOp",EDGE,"E13.18.3"),sQuery(id+"F0.wireOp",EDGE,"E13.18.4"),sQuery(id+"F0.wireOp",EDGE,"E13.18.5"),sQuery(id+"F0.wireOp",EDGE,"E13.18.6"),sQuery(id+"F0.wireOp",EDGE,"E13.18.7"),sQuery(id+"F0.wireOp",EDGE,"E13.18.8"),sQuery(id+"F0.wireOp",EDGE,"E13.18.9"),sQuery(id+"F0.wireOp",EDGE,"E13.18.10"),sQuery(id+"F0.wireOp",EDGE,"E13.18.11"),sQuery(id+"F0.wireOp",EDGE,"E13.19.0"),sQuery(id+"F0.wireOp",EDGE,"E13.19.1"),sQuery(id+"F0.wireOp",EDGE,"E13.19.2"),sQuery(id+"F0.wireOp",EDGE,"E13.19.3"),sQuery(id+"F0.wireOp",EDGE,"E13.19.4"),sQuery(id+"F0.wireOp",EDGE,"E13.19.5"),sQuery(id+"F0.wireOp",EDGE,"E13.19.6"),sQuery(id+"F0.wireOp",EDGE,"E13.19.7"),sQuery(id+"F0.wireOp",EDGE,"E13.19.8"),sQuery(id+"F0.wireOp",EDGE,"E13.19.9"),sQuery(id+"F0.wireOp",EDGE,"E13.19.10"),sQuery(id+"F0.wireOp",EDGE,"E13.19.11"),sQuery(id+"F0.wireOp",EDGE,"E13.20.0"),sQuery(id+"F0.wireOp",EDGE,"E13.20.1"),sQuery(id+"F0.wireOp",EDGE,"E13.20.2"),sQuery(id+"F0.wireOp",EDGE,"E13.20.3"),sQuery(id+"F0.wireOp",EDGE,"E13.20.4"),sQuery(id+"F0.wireOp",EDGE,"E13.20.5"),sQuery(id+"F0.wireOp",EDGE,"E13.20.6"),sQuery(id+"F0.wireOp",EDGE,"E13.20.7"),sQuery(id+"F0.wireOp",EDGE,"E13.20.8"),sQuery(id+"F0.wireOp",EDGE,"E13.20.9"),sQuery(id+"F0.wireOp",EDGE,"E13.20.10"),sQuery(id+"F0.wireOp",EDGE,"E13.20.11"),sQuery(id+"F0.wireOp",EDGE,"E13.21.0"),sQuery(id+"F0.wireOp",EDGE,"E13.21.1"),sQuery(id+"F0.wireOp",EDGE,"E13.21.2"),sQuery(id+"F0.wireOp",EDGE,"E13.21.3"),sQuery(id+"F0.wireOp",EDGE,"E13.21.4"),sQuery(id+"F0.wireOp",EDGE,"E13.21.5"),sQuery(id+"F0.wireOp",EDGE,"E13.21.6"),sQuery(id+"F0.wireOp",EDGE,"E13.21.7"),sQuery(id+"F0.wireOp",EDGE,"E13.21.8"),sQuery(id+"F0.wireOp",EDGE,"E13.21.9"),sQuery(id+"F0.wireOp",EDGE,"E13.21.10"),sQuery(id+"F0.wireOp",EDGE,"E13.21.11"),sQuery(id+"F0.wireOp",EDGE,"E13.22.0"),sQuery(id+"F0.wireOp",EDGE,"E13.22.1"),sQuery(id+"F0.wireOp",EDGE,"E13.22.2"),sQuery(id+"F0.wireOp",EDGE,"E13.22.3"),sQuery(id+"F0.wireOp",EDGE,"E13.22.4"),sQuery(id+"F0.wireOp",EDGE,"E13.22.5"),sQuery(id+"F0.wireOp",EDGE,"E13.22.6"),sQuery(id+"F0.wireOp",EDGE,"E13.22.7"),sQuery(id+"F0.wireOp",EDGE,"E13.22.8"),sQuery(id+"F0.wireOp",EDGE,"E13.22.9"),sQuery(id+"F0.wireOp",EDGE,"E13.22.10"),sQuery(id+"F0.wireOp",EDGE,"E13.22.11"),sQuery(id+"F0.wireOp",EDGE,"E13.23.0"),sQuery(id+"F0.wireOp",EDGE,"E13.23.1"),sQuery(id+"F0.wireOp",EDGE,"E13.23.2"),sQuery(id+"F0.wireOp",EDGE,"E13.23.3"),sQuery(id+"F0.wireOp",EDGE,"E13.23.4"),sQuery(id+"F0.wireOp",EDGE,"E13.23.5"),sQuery(id+"F0.wireOp",EDGE,"E13.23.6"),sQuery(id+"F0.wireOp",EDGE,"E13.23.7"),sQuery(id+"F0.wireOp",EDGE,"E13.23.8"),sQuery(id+"F0.wireOp",EDGE,"E13.23.9"),sQuery(id+"F0.wireOp",EDGE,"E13.23.10"),sQuery(id+"F0.wireOp",EDGE,"E13.23.11"),sQuery(id+"F0.wireOp",EDGE,"E14.trimOffspring"),sQuery(id+"F0.wireOp",EDGE,"E15.trimOffspring"),sQuery(id+"F0.wireOp",EDGE,"E16.trimOffspring"),sQuery(id+"F0.wireOp",EDGE,"E17.trimOffspring"),sQuery(id+"F0.wireOp",EDGE,"E18.trimOffspring"),sQuery(id+"F0.wireOp",EDGE,"E19.trimOffspring"),sQuery(id+"F0.wireOp",EDGE,"E20.trimOffspring"),sQuery(id+"F0.wireOp",EDGE,"E21.trimOffspring"),sQuery(id+"F0.wireOp",EDGE,"E22.trimOffspring"),sQuery(id+"F0.wireOp",EDGE,"E23.trimOffspring"),sQuery(id+"F0.wireOp",EDGE,"E24.trimOffspring"),sQuery(id+"F0.wireOp",EDGE,"E25.trimOffspring"),sQuery(id+"F0.wireOp",EDGE,"E26.trimOffspring"),sQuery(id+"F0.wireOp",EDGE,"E27.trimOffspring"),sQuery(id+"F0.wireOp",EDGE,"E28.trimOffspring"),sQuery(id+"F0.wireOp",EDGE,"E29.trimOffspring"),sQuery(id+"F0.wireOp",EDGE,"E30.trimOffspring"),sQuery(id+"F0.wireOp",EDGE,"E31.trimOffspring"),sQuery(id+"F0.wireOp",EDGE,"E32.trimOffspring"),sQuery(id+"F0.wireOp",EDGE,"E33.trimOffspring"),sQuery(id+"F0.wireOp",EDGE,"E34.trimOffspring"),sQuery(id+"F0.wireOp",EDGE,"E35.trimOffspring"),sQuery(id+"F0.wireOp",EDGE,"E36.trimOffspring")])],"isStart":false});
            var sketch = newSketch(context, id + "F2", { "sketchPlane" : qUnion([Q0])});
            skCircle(sketch, "E37", {"center": v(0, 0) * mm, "radius": 6.35 * mm});
            skSolve(sketch);
        }
        {
            var Q0;
            Q0 = qSketchRegion(id + "F2", true);
            extrude(context, id + "F3", {"entities" : qUnion([Q0]), "operationType" : NewBodyOperationType.REMOVE, "endBound" : BoundingType.THROUGH_ALL, "oppositeDirection" : true, "depth" : 25.4 * mm});
        }
    });
